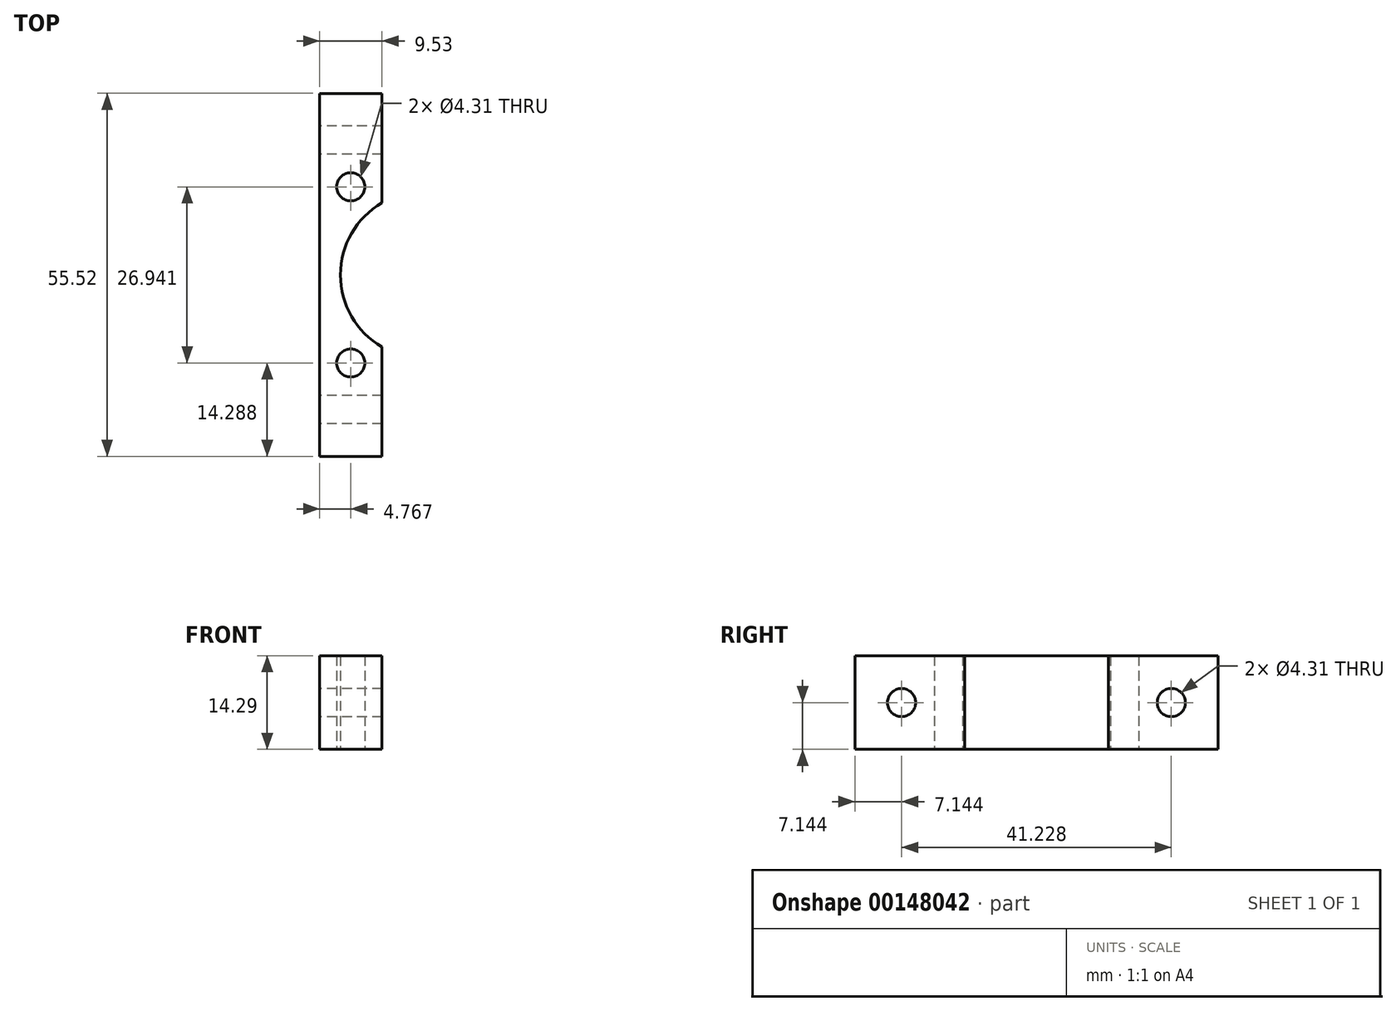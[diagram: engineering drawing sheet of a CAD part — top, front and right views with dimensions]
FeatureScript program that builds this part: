
annotation { "Feature Type Name" : "Feature", "Feature Type Description" : "" }
export const myFeature = defineFeature(function(context is Context, id is Id, definition is map)
    precondition{}
    {
        {
            var Q0;
            Q0=qCreatedBy(makeId("Top.planeOp"),FACE);
            var sketch = newSketch(context, id + "F0", { "sketchPlane" : qUnion([Q0])});
            skArc(sketch, "E0", {"start": v(0, 22) * mm, "mid": v(-6.35, 11) * mm, "end": v(0, 0) * mm});
            skLineSegment(sketch, "E1", {"start": v(0, 0) * mm, "end": v(0, 22) * mm, "construction": true});
            skLineSegment(sketch, "E2", {"start": v(0, 11) * mm, "end": v(6.35, 11) * mm, "construction": true});
            skCircle(sketch, "E3", {"center": v(6.35, 11) * mm, "radius": 11.11 * mm, "construction": true});
            skLineSegment(sketch, "E4", {"start": v(0, 11) * mm, "end": v(-6.35, 11) * mm, "construction": true});
            skLineSegment(sketch, "E5", {"start": v(0, 0) * mm, "end": v(0, -16.76) * mm});
            skLineSegment(sketch, "E6", {"start": v(0, -16.76) * mm, "end": v(-9.53, -16.76) * mm});
            skLineSegment(sketch, "E7", {"start": v(-9.53, -16.76) * mm, "end": v(-9.53, 38.76) * mm});
            skLineSegment(sketch, "E8", {"start": v(-9.53, 38.76) * mm, "end": v(0, 38.76) * mm});
            skLineSegment(sketch, "E9", {"start": v(0, 38.76) * mm, "end": v(0, 22) * mm});
            skCircle(sketch, "E10", {"center": v(-4.76, 24.47) * mm, "radius": 4.76 * mm, "construction": true});
            skLineSegment(sketch, "E11", {"start": v(-4.76, 24.47) * mm, "end": v(-4.76, 34) * mm, "construction": true});
            skLineSegment(sketch, "E12", {"start": v(-4.76, 34) * mm, "end": v(-4.76, 38.76) * mm, "construction": true});
            skCircle(sketch, "E13", {"center": v(-4.76, 24.47) * mm, "radius": 2.15 * mm});
            skCircle(sketch, "E14", {"center": v(-4.76, -2.47) * mm, "radius": 4.76 * mm, "construction": true});
            skCircle(sketch, "E15", {"center": v(-4.76, -2.47) * mm, "radius": 2.15 * mm});
            skSolve(sketch);
        }
        {
            var Q0;
            Q0=qSketchRegion(id+"F0",true);
            extrude(context, id + "F1", {"entities" : qUnion([Q0]), "depth" : 14.29 * mm});
        }
        {
            var Q0;
            Q0=makeQuery(id+"F1.opExtrude","SWEPT_FACE",FACE,{"disambiguationData":[OSD([sQuery(id+"F0.wireOp",EDGE,"E7")])]});
            var sketch = newSketch(context, id + "F2", { "sketchPlane" : qUnion([Q0])});
            skLineSegment(sketch, "E16.bottom", {"start": v(16.76, 7.14) * mm, "end": v(9.62, 7.14) * mm, "construction": true});
            skLineSegment(sketch, "E16.top", {"start": v(16.76, 0) * mm, "end": v(9.62, 0) * mm, "construction": true});
            skLineSegment(sketch, "E16.left", {"start": v(16.76, 7.14) * mm, "end": v(16.76, 0) * mm, "construction": true});
            skLineSegment(sketch, "E16.right", {"start": v(9.62, 7.14) * mm, "end": v(9.62, 0) * mm, "construction": true});
            skLineSegment(sketch, "E17.bottom", {"start": v(-38.76, 7.14) * mm, "end": v(-31.61, 7.14) * mm, "construction": true});
            skLineSegment(sketch, "E17.top", {"start": v(-38.76, 0) * mm, "end": v(-31.61, 0) * mm, "construction": true});
            skLineSegment(sketch, "E17.left", {"start": v(-38.76, 7.14) * mm, "end": v(-38.76, 0) * mm, "construction": true});
            skLineSegment(sketch, "E17.right", {"start": v(-31.61, 7.14) * mm, "end": v(-31.61, 0) * mm, "construction": true});
            skCircle(sketch, "E18", {"center": v(9.62, 7.14) * mm, "radius": 2.15 * mm});
            skCircle(sketch, "E19", {"center": v(-31.61, 7.14) * mm, "radius": 2.15 * mm});
            skSolve(sketch);
        }
        {
            var Q0;
            Q0=qSketchRegion(id+"F2",true);
            var Q1;
            Q1=makeQuery(id+"F1.opExtrude","SWEPT_FACE",FACE,{"disambiguationData":[OSD([sQuery(id+"F0.wireOp",EDGE,"E5")])]});
            extrude(context, id + "F3", {"entities" : qUnion([Q0]), "operationType" : NewBodyOperationType.REMOVE, "endBound" : BoundingType.UP_TO_SURFACE, "oppositeDirection" : true, "endBoundEntityFace" : qUnion([Q1]), "depth" : 25.4 * mm});
        }
    });
